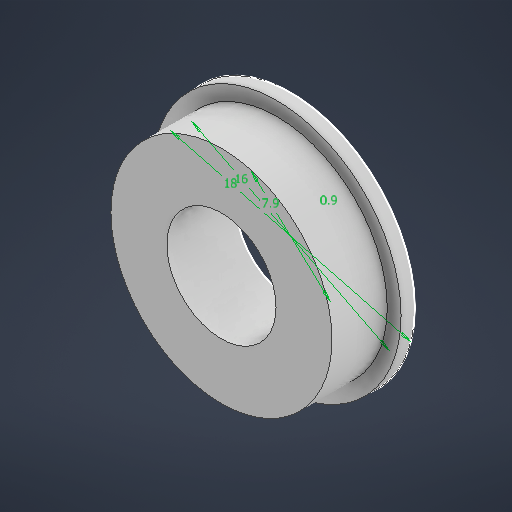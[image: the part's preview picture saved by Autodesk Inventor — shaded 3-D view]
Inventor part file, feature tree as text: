
AUTODESK INVENTOR PART (.ipt)
format: ipt  version: 2025.1 (Build 291241000, 241)  size: 218,624 bytes
history: native  units: mm
features: extrude x2, sketch x1
ambient origin geometry x8: Origin, YZ Plane, XZ Plane, XY Plane, X Axis, Y Axis, Z Axis, Center Point
bodies: Solid1 (feature_tree)
feature tree (3):
  sketch  "Sketch1"  dims[d0=7.9mm d1=16.0mm d2=18.0mm d3=1.0mm d4=0.0mm d5=5.0mm d6=0.0mm d7=0.9mm]
  extrude  "Extrusion1"  Depth=5.0mm
  extrude  "Extrusion2"  Depth=5.0mm
